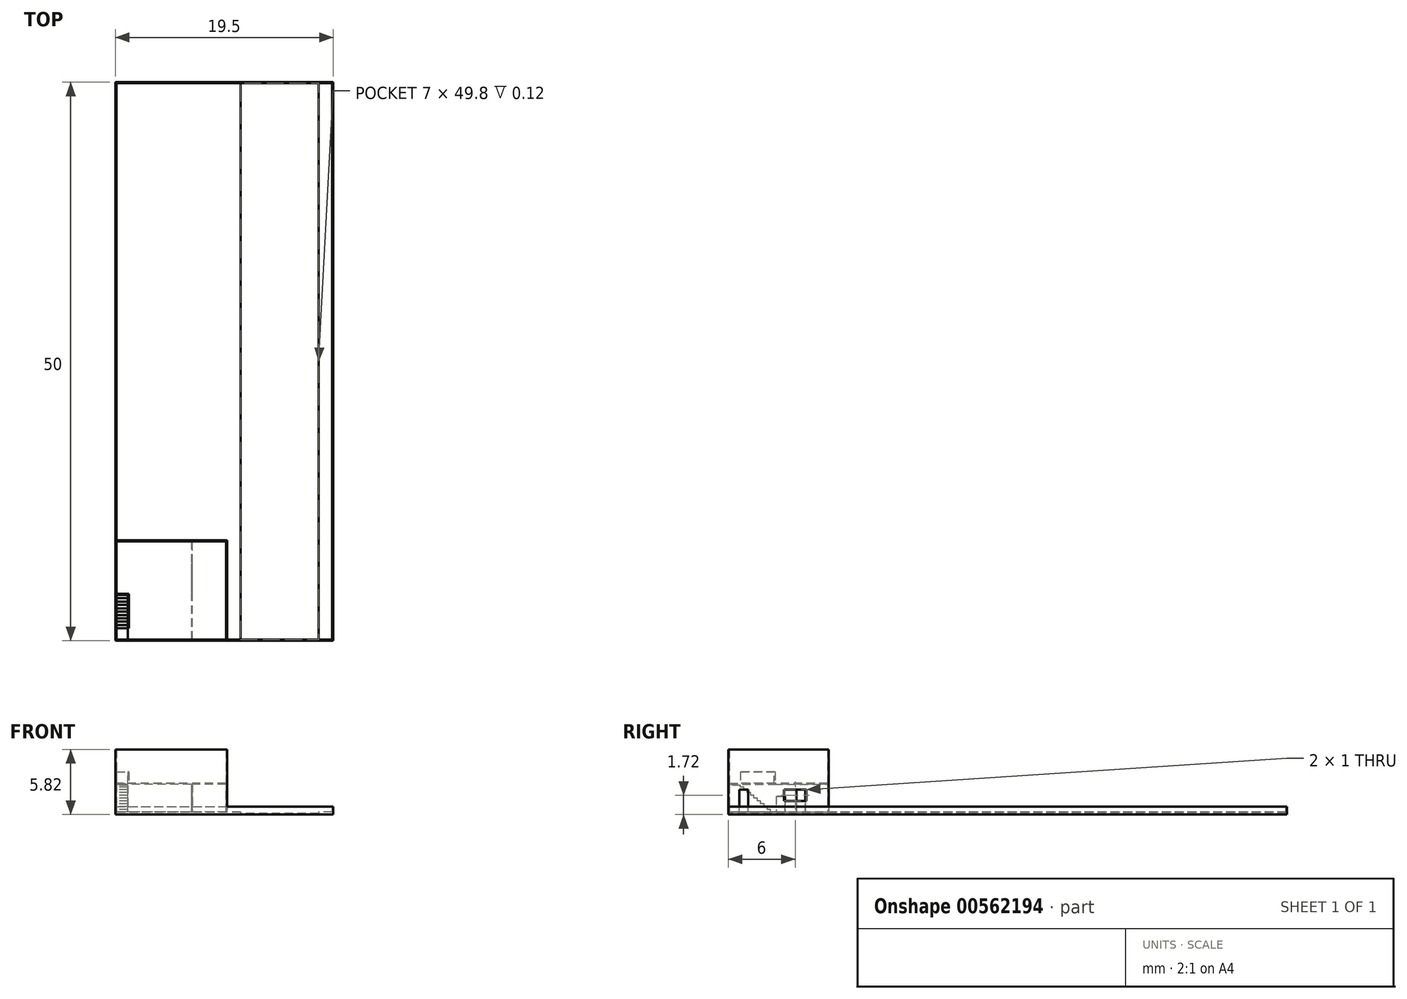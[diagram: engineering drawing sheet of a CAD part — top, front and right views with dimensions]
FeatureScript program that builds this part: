
annotation { "Feature Type Name" : "Feature", "Feature Type Description" : "" }
export const myFeature = defineFeature(function(context is Context, id is Id, definition is map)
    precondition{}
    {
        {
            var Q0;
            Q0=qCreatedBy(makeId("Top.planeOp"),FACE);
            var sketch = newSketch(context, id + "F0", { "sketchPlane" : qUnion([Q0])});
            skLineSegment(sketch, "E0.bottom", {"start": v(0, 0) * mm, "end": v(19.5, 0) * mm});
            skLineSegment(sketch, "E0.top", {"start": v(0, 50) * mm, "end": v(19.5, 50) * mm});
            skLineSegment(sketch, "E0.left", {"start": v(0, 0) * mm, "end": v(0, 50) * mm});
            skLineSegment(sketch, "E0.right", {"start": v(19.5, 0) * mm, "end": v(19.5, 50) * mm});
            skLineSegment(sketch, "E1", {"start": v(11.2, 50) * mm, "end": v(11.2, 0) * mm});
            skLineSegment(sketch, "E2", {"start": v(18.2, 50) * mm, "end": v(18.2, 0) * mm});
            skLineSegment(sketch, "E3", {"start": v(10, 0) * mm, "end": v(10, 50) * mm});
            skLineSegment(sketch, "E4", {"start": v(0, 49.9) * mm, "end": v(19.5, 49.9) * mm});
            skLineSegment(sketch, "E5", {"start": v(19.4, 50) * mm, "end": v(19.4, 0) * mm});
            skLineSegment(sketch, "E6", {"start": v(19.5, 0.1) * mm, "end": v(0, 0.1) * mm});
            skSolve(sketch);
        }
        {
            var Q0;
            {var subQ0=sQuery(id+"F0.wireOp",EDGE,"E4");var subQ1=sQuery(id+"F0.wireOp",EDGE,"E1");var subQ2=makeQuery(id+"F0.imprint","INTERSECT",VERTEX,{"derivedFrom":[subQ1,subQ0]});Q0=makeQuery(id+"F0.imprint","IMPRINT",FACE,{"disambiguationData":[TD([[makeQuery(id+"F0.imprint","IMPRINT",EDGE,{"disambiguationData":[TD([[subQ2,-1.0]])],"derivedFrom":subQ1}),-1.0]])]});}
            var Q1;
            {var subQ0=sQuery(id+"F0.wireOp",EDGE,"E4");var subQ1=sQuery(id+"F0.wireOp",EDGE,"E0.left");var subQ2=makeQuery(id+"F0.imprint","INTERSECT",VERTEX,{"derivedFrom":[subQ1,subQ0]});Q1=makeQuery(id+"F0.imprint","IMPRINT",FACE,{"disambiguationData":[TD([[makeQuery(id+"F0.imprint","IMPRINT",EDGE,{"disambiguationData":[TD([[subQ2,1.0]])],"derivedFrom":subQ1}),-1.0]])]});}
            var Q2;
            {var subQ0=sQuery(id+"F0.wireOp",EDGE,"E4");var subQ1=sQuery(id+"F0.wireOp",EDGE,"E2");var subQ2=makeQuery(id+"F0.imprint","INTERSECT",VERTEX,{"derivedFrom":[subQ1,subQ0]});Q2=makeQuery(id+"F0.imprint","IMPRINT",FACE,{"disambiguationData":[TD([[makeQuery(id+"F0.imprint","IMPRINT",EDGE,{"disambiguationData":[TD([[subQ2,-1.0]])],"derivedFrom":subQ1}),1.0]])]});}
            extrude(context, id + "F1", {"entities" : qUnion([Q0, Q1, Q2]), "depth" : 0.12 * mm, "offsetDistance" : 25 * mm});
        }
        {
            var Q0;
            {var subQ0=sQuery(id+"F0.wireOp",EDGE,"E4");var subQ1=sQuery(id+"F0.wireOp",EDGE,"E0.left");var subQ2=makeQuery(id+"F0.imprint","INTERSECT",VERTEX,{"derivedFrom":[subQ1,subQ0]});Q0=makeQuery(id+"F0.imprint","IMPRINT",FACE,{"disambiguationData":[TD([[makeQuery(id+"F0.imprint","IMPRINT",EDGE,{"disambiguationData":[TD([[subQ2,1.0]])],"derivedFrom":subQ1}),-1.0]])]});}
            var Q1;
            {var subQ0=sQuery(id+"F0.wireOp",EDGE,"E4");var subQ1=sQuery(id+"F0.wireOp",EDGE,"E1");var subQ2=makeQuery(id+"F0.imprint","INTERSECT",VERTEX,{"derivedFrom":[subQ1,subQ0]});Q1=makeQuery(id+"F0.imprint","IMPRINT",FACE,{"disambiguationData":[TD([[makeQuery(id+"F0.imprint","IMPRINT",EDGE,{"disambiguationData":[TD([[subQ2,-1.0]])],"derivedFrom":subQ1}),-1.0]])]});}
            var Q2;
            {var subQ0=sQuery(id+"F0.wireOp",EDGE,"E4");var subQ1=sQuery(id+"F0.wireOp",EDGE,"E2");var subQ2=makeQuery(id+"F0.imprint","INTERSECT",VERTEX,{"derivedFrom":[subQ1,subQ0]});Q2=makeQuery(id+"F0.imprint","IMPRINT",FACE,{"disambiguationData":[TD([[makeQuery(id+"F0.imprint","IMPRINT",EDGE,{"disambiguationData":[TD([[subQ2,-1.0]])],"derivedFrom":subQ1}),1.0]])]});}
            var Q3;
            {var subQ0=sQuery(id+"F0.wireOp",EDGE,"E4");var subQ1=sQuery(id+"F0.wireOp",EDGE,"E1");var subQ2=makeQuery(id+"F0.imprint","INTERSECT",VERTEX,{"derivedFrom":[subQ1,subQ0]});Q3=makeQuery(id+"F0.imprint","IMPRINT",FACE,{"disambiguationData":[TD([[makeQuery(id+"F0.imprint","IMPRINT",EDGE,{"disambiguationData":[TD([[subQ2,-1.0]])],"derivedFrom":subQ1}),1.0]])]});}
            var Q4;
            {var subQ0=sQuery(id+"F0.wireOp",EDGE,"E1");var subQ1=sQuery(id+"F0.wireOp",EDGE,"E0.bottom");var subQ2=makeQuery(id+"F0.imprint","INTERSECT",VERTEX,{"derivedFrom":[subQ1,subQ0]});Q4=makeQuery(id+"F0.imprint","IMPRINT",FACE,{"disambiguationData":[TD([[makeQuery(id+"F0.imprint","IMPRINT",EDGE,{"disambiguationData":[TD([[subQ2,-1.0]])],"derivedFrom":subQ1}),1.0]])]});}
            var Q5;
            {var subQ0=sQuery(id+"F0.wireOp",EDGE,"E1");var subQ1=sQuery(id+"F0.wireOp",EDGE,"E0.bottom");var subQ2=makeQuery(id+"F0.imprint","INTERSECT",VERTEX,{"derivedFrom":[subQ1,subQ0]});Q5=makeQuery(id+"F0.imprint","IMPRINT",FACE,{"disambiguationData":[TD([[makeQuery(id+"F0.imprint","IMPRINT",EDGE,{"disambiguationData":[TD([[subQ2,1.0]])],"derivedFrom":subQ1}),1.0]])]});}
            var Q6;
            {var subQ0=sQuery(id+"F0.wireOp",EDGE,"E2");var subQ1=sQuery(id+"F0.wireOp",EDGE,"E0.bottom");var subQ2=makeQuery(id+"F0.imprint","INTERSECT",VERTEX,{"derivedFrom":[subQ1,subQ0]});Q6=makeQuery(id+"F0.imprint","IMPRINT",FACE,{"disambiguationData":[TD([[makeQuery(id+"F0.imprint","IMPRINT",EDGE,{"disambiguationData":[TD([[subQ2,-1.0]])],"derivedFrom":subQ1}),1.0]])]});}
            var Q7;
            {var subQ0=sQuery(id+"F0.wireOp",EDGE,"E4");var subQ1=sQuery(id+"F0.wireOp",EDGE,"E0.right");var subQ2=makeQuery(id+"F0.imprint","INTERSECT",VERTEX,{"derivedFrom":[subQ1,subQ0]});Q7=makeQuery(id+"F0.imprint","IMPRINT",FACE,{"disambiguationData":[TD([[makeQuery(id+"F0.imprint","IMPRINT",EDGE,{"disambiguationData":[TD([[subQ2,1.0]])],"derivedFrom":subQ1}),1.0]])]});}
            var Q8;
            {var subQ0=sQuery(id+"F0.wireOp",EDGE,"E0.right");var subQ1=sQuery(id+"F0.wireOp",EDGE,"E0.bottom");var subQ2=makeQuery(id+"F0.imprint","INTERSECT",VERTEX,{"derivedFrom":[subQ1,subQ0]});Q8=makeQuery(id+"F0.imprint","IMPRINT",FACE,{"disambiguationData":[TD([[makeQuery(id+"F0.imprint","IMPRINT",EDGE,{"disambiguationData":[TD([[subQ2,1.0]])],"derivedFrom":subQ1}),1.0]])]});}
            var Q9;
            {var subQ0=sQuery(id+"F0.wireOp",EDGE,"E0.left");var subQ1=sQuery(id+"F0.wireOp",EDGE,"E0.bottom");var subQ2=makeQuery(id+"F0.imprint","INTERSECT",VERTEX,{"derivedFrom":[subQ1,subQ0]});Q9=makeQuery(id+"F0.imprint","IMPRINT",FACE,{"disambiguationData":[TD([[makeQuery(id+"F0.imprint","IMPRINT",EDGE,{"disambiguationData":[TD([[subQ2,-1.0]])],"derivedFrom":subQ1}),1.0]])]});}
            var Q10;
            {var subQ0=sQuery(id+"F0.wireOp",EDGE,"E0.right");var subQ1=sQuery(id+"F0.wireOp",EDGE,"E0.top");var subQ2=makeQuery(id+"F0.imprint","INTERSECT",VERTEX,{"derivedFrom":[subQ1,subQ0]});Q10=makeQuery(id+"F0.imprint","IMPRINT",FACE,{"disambiguationData":[TD([[makeQuery(id+"F0.imprint","IMPRINT",EDGE,{"disambiguationData":[TD([[subQ2,1.0]])],"derivedFrom":subQ1}),-1.0]])]});}
            var Q11;
            {var subQ0=sQuery(id+"F0.wireOp",EDGE,"E2");var subQ1=sQuery(id+"F0.wireOp",EDGE,"E0.top");var subQ2=makeQuery(id+"F0.imprint","INTERSECT",VERTEX,{"derivedFrom":[subQ1,subQ0]});Q11=makeQuery(id+"F0.imprint","IMPRINT",FACE,{"disambiguationData":[TD([[makeQuery(id+"F0.imprint","IMPRINT",EDGE,{"disambiguationData":[TD([[subQ2,-1.0]])],"derivedFrom":subQ1}),-1.0]])]});}
            var Q12;
            {var subQ0=sQuery(id+"F0.wireOp",EDGE,"E1");var subQ1=sQuery(id+"F0.wireOp",EDGE,"E0.top");var subQ2=makeQuery(id+"F0.imprint","INTERSECT",VERTEX,{"derivedFrom":[subQ1,subQ0]});Q12=makeQuery(id+"F0.imprint","IMPRINT",FACE,{"disambiguationData":[TD([[makeQuery(id+"F0.imprint","IMPRINT",EDGE,{"disambiguationData":[TD([[subQ2,-1.0]])],"derivedFrom":subQ1}),-1.0]])]});}
            var Q13;
            {var subQ0=sQuery(id+"F0.wireOp",EDGE,"E1");var subQ1=sQuery(id+"F0.wireOp",EDGE,"E0.top");var subQ2=makeQuery(id+"F0.imprint","INTERSECT",VERTEX,{"derivedFrom":[subQ1,subQ0]});Q13=makeQuery(id+"F0.imprint","IMPRINT",FACE,{"disambiguationData":[TD([[makeQuery(id+"F0.imprint","IMPRINT",EDGE,{"disambiguationData":[TD([[subQ2,1.0]])],"derivedFrom":subQ1}),-1.0]])]});}
            var Q14;
            {var subQ0=sQuery(id+"F0.wireOp",EDGE,"E0.left");var subQ1=sQuery(id+"F0.wireOp",EDGE,"E0.top");var subQ2=makeQuery(id+"F0.imprint","INTERSECT",VERTEX,{"derivedFrom":[subQ1,subQ0]});Q14=makeQuery(id+"F0.imprint","IMPRINT",FACE,{"disambiguationData":[TD([[makeQuery(id+"F0.imprint","IMPRINT",EDGE,{"disambiguationData":[TD([[subQ2,-1.0]])],"derivedFrom":subQ1}),-1.0]])]});}
            var Q15;
            Q15=makeQuery(id+"F1.opExtrude","CAP_FACE",FACE,{"disambiguationData":[OSD([sQuery(id+"F0.wireOp",EDGE,"E2"),sQuery(id+"F0.wireOp",EDGE,"E4"),sQuery(id+"F0.wireOp",EDGE,"E5"),sQuery(id+"F0.wireOp",EDGE,"E6")])],"isStart":false});
            var Q16;
            Q16=makeQuery(id+"F1.opExtrude","CAP_FACE",FACE,{"disambiguationData":[OSD([sQuery(id+"F0.wireOp",EDGE,"E0.left"),sQuery(id+"F0.wireOp",EDGE,"E1"),sQuery(id+"F0.wireOp",EDGE,"E4"),sQuery(id+"F0.wireOp",EDGE,"E6")])],"isStart":false});
            extrude(context, id + "F2", {"entities" : qUnion([Q0, Q1, Q2, Q3, Q4, Q5, Q6, Q7, Q8, Q9, Q10, Q11, Q12, Q13, Q14, Q15, Q16]), "operationType" : NewBodyOperationType.ADD, "oppositeDirection" : true, "depth" : 0.1 * mm, "offsetDistance" : 25 * mm});
        }
        {
            var Q0;
            {var subQ0=sQuery(id+"F0.wireOp",EDGE,"E1");var subQ1=sQuery(id+"F0.wireOp",EDGE,"E0.top");var subQ2=makeQuery(id+"F0.imprint","INTERSECT",VERTEX,{"derivedFrom":[subQ1,subQ0]});Q0=makeQuery(id+"F0.imprint","IMPRINT",FACE,{"disambiguationData":[TD([[makeQuery(id+"F0.imprint","IMPRINT",EDGE,{"disambiguationData":[TD([[subQ2,1.0]])],"derivedFrom":subQ1}),-1.0]])]});}
            var Q1;
            {var subQ0=sQuery(id+"F0.wireOp",EDGE,"E0.left");var subQ1=sQuery(id+"F0.wireOp",EDGE,"E0.top");var subQ2=makeQuery(id+"F0.imprint","INTERSECT",VERTEX,{"derivedFrom":[subQ1,subQ0]});Q1=makeQuery(id+"F0.imprint","IMPRINT",FACE,{"disambiguationData":[TD([[makeQuery(id+"F0.imprint","IMPRINT",EDGE,{"disambiguationData":[TD([[subQ2,-1.0]])],"derivedFrom":subQ1}),-1.0]])]});}
            var Q2;
            {var subQ0=sQuery(id+"F0.wireOp",EDGE,"E1");var subQ1=sQuery(id+"F0.wireOp",EDGE,"E0.top");var subQ2=makeQuery(id+"F0.imprint","INTERSECT",VERTEX,{"derivedFrom":[subQ1,subQ0]});Q2=makeQuery(id+"F0.imprint","IMPRINT",FACE,{"disambiguationData":[TD([[makeQuery(id+"F0.imprint","IMPRINT",EDGE,{"disambiguationData":[TD([[subQ2,-1.0]])],"derivedFrom":subQ1}),-1.0]])]});}
            var Q3;
            {var subQ0=sQuery(id+"F0.wireOp",EDGE,"E2");var subQ1=sQuery(id+"F0.wireOp",EDGE,"E0.top");var subQ2=makeQuery(id+"F0.imprint","INTERSECT",VERTEX,{"derivedFrom":[subQ1,subQ0]});Q3=makeQuery(id+"F0.imprint","IMPRINT",FACE,{"disambiguationData":[TD([[makeQuery(id+"F0.imprint","IMPRINT",EDGE,{"disambiguationData":[TD([[subQ2,-1.0]])],"derivedFrom":subQ1}),-1.0]])]});}
            var Q4;
            {var subQ0=sQuery(id+"F0.wireOp",EDGE,"E4");var subQ1=sQuery(id+"F0.wireOp",EDGE,"E0.right");var subQ2=makeQuery(id+"F0.imprint","INTERSECT",VERTEX,{"derivedFrom":[subQ1,subQ0]});Q4=makeQuery(id+"F0.imprint","IMPRINT",FACE,{"disambiguationData":[TD([[makeQuery(id+"F0.imprint","IMPRINT",EDGE,{"disambiguationData":[TD([[subQ2,1.0]])],"derivedFrom":subQ1}),1.0]])]});}
            var Q5;
            {var subQ0=sQuery(id+"F0.wireOp",EDGE,"E0.right");var subQ1=sQuery(id+"F0.wireOp",EDGE,"E0.top");var subQ2=makeQuery(id+"F0.imprint","INTERSECT",VERTEX,{"derivedFrom":[subQ1,subQ0]});Q5=makeQuery(id+"F0.imprint","IMPRINT",FACE,{"disambiguationData":[TD([[makeQuery(id+"F0.imprint","IMPRINT",EDGE,{"disambiguationData":[TD([[subQ2,1.0]])],"derivedFrom":subQ1}),-1.0]])]});}
            var Q6;
            {var subQ0=sQuery(id+"F0.wireOp",EDGE,"E0.right");var subQ1=sQuery(id+"F0.wireOp",EDGE,"E0.bottom");var subQ2=makeQuery(id+"F0.imprint","INTERSECT",VERTEX,{"derivedFrom":[subQ1,subQ0]});Q6=makeQuery(id+"F0.imprint","IMPRINT",FACE,{"disambiguationData":[TD([[makeQuery(id+"F0.imprint","IMPRINT",EDGE,{"disambiguationData":[TD([[subQ2,1.0]])],"derivedFrom":subQ1}),1.0]])]});}
            var Q7;
            {var subQ0=sQuery(id+"F0.wireOp",EDGE,"E2");var subQ1=sQuery(id+"F0.wireOp",EDGE,"E0.bottom");var subQ2=makeQuery(id+"F0.imprint","INTERSECT",VERTEX,{"derivedFrom":[subQ1,subQ0]});Q7=makeQuery(id+"F0.imprint","IMPRINT",FACE,{"disambiguationData":[TD([[makeQuery(id+"F0.imprint","IMPRINT",EDGE,{"disambiguationData":[TD([[subQ2,-1.0]])],"derivedFrom":subQ1}),1.0]])]});}
            var Q8;
            {var subQ0=sQuery(id+"F0.wireOp",EDGE,"E1");var subQ1=sQuery(id+"F0.wireOp",EDGE,"E0.bottom");var subQ2=makeQuery(id+"F0.imprint","INTERSECT",VERTEX,{"derivedFrom":[subQ1,subQ0]});Q8=makeQuery(id+"F0.imprint","IMPRINT",FACE,{"disambiguationData":[TD([[makeQuery(id+"F0.imprint","IMPRINT",EDGE,{"disambiguationData":[TD([[subQ2,-1.0]])],"derivedFrom":subQ1}),1.0]])]});}
            var Q9;
            {var subQ0=sQuery(id+"F0.wireOp",EDGE,"E0.left");var subQ1=sQuery(id+"F0.wireOp",EDGE,"E0.bottom");var subQ2=makeQuery(id+"F0.imprint","INTERSECT",VERTEX,{"derivedFrom":[subQ1,subQ0]});Q9=makeQuery(id+"F0.imprint","IMPRINT",FACE,{"disambiguationData":[TD([[makeQuery(id+"F0.imprint","IMPRINT",EDGE,{"disambiguationData":[TD([[subQ2,-1.0]])],"derivedFrom":subQ1}),1.0]])]});}
            var Q10;
            {var subQ0=sQuery(id+"F0.wireOp",EDGE,"E1");var subQ1=sQuery(id+"F0.wireOp",EDGE,"E0.bottom");var subQ2=makeQuery(id+"F0.imprint","INTERSECT",VERTEX,{"derivedFrom":[subQ1,subQ0]});Q10=makeQuery(id+"F0.imprint","IMPRINT",FACE,{"disambiguationData":[TD([[makeQuery(id+"F0.imprint","IMPRINT",EDGE,{"disambiguationData":[TD([[subQ2,1.0]])],"derivedFrom":subQ1}),1.0]])]});}
            extrude(context, id + "F3", {"entities" : qUnion([Q0, Q1, Q2, Q3, Q4, Q5, Q6, Q7, Q8, Q9, Q10]), "operationType" : NewBodyOperationType.ADD, "depth" : 0.6 * mm, "offsetDistance" : 25 * mm});
        }
        {
            var Q0;
            Q0=makeQuery(id+"F1.opExtrude","CAP_FACE",FACE,{"disambiguationData":[OSD([sQuery(id+"F0.wireOp",EDGE,"E0.left"),sQuery(id+"F0.wireOp",EDGE,"E1"),sQuery(id+"F0.wireOp",EDGE,"E4"),sQuery(id+"F0.wireOp",EDGE,"E6")])],"isStart":false});
            var sketch = newSketch(context, id + "F4", { "sketchPlane" : qUnion([Q0])});
            skLineSegment(sketch, "E7.bottom", {"start": v(10, 0) * mm, "end": v(0, 0) * mm});
            skLineSegment(sketch, "E7.top", {"start": v(10, 9) * mm, "end": v(0, 9) * mm});
            skLineSegment(sketch, "E7.left", {"start": v(10, 0) * mm, "end": v(10, 9) * mm});
            skLineSegment(sketch, "E7.right", {"start": v(0, 0) * mm, "end": v(0, 9) * mm});
            skLineSegment(sketch, "E8.0", {"start": v(0.1, 0.1) * mm, "end": v(0.1, 8.9) * mm});
            skLineSegment(sketch, "E8.1", {"start": v(9.9, 0.1) * mm, "end": v(0.1, 0.1) * mm});
            skLineSegment(sketch, "E8.2", {"start": v(9.9, 0.1) * mm, "end": v(9.9, 8.9) * mm});
            skLineSegment(sketch, "E8.3", {"start": v(9.9, 8.9) * mm, "end": v(0.1, 8.9) * mm});
            skLineSegment(sketch, "E9", {"start": v(6.9, 0.1) * mm, "end": v(6.9, 8.9) * mm});
            skLineSegment(sketch, "E10", {"start": v(6.8, 8.9) * mm, "end": v(6.8, 0.1) * mm});
            skSolve(sketch);
        }
        {
            var Q0;
            Q0 = qSketchRegion(id + "F4", true);
            var Q1;
            {var subQ0=sQuery(id+"F4.wireOp",EDGE,"E9");Q1=makeQuery(id+"F4.imprint","IMPRINT",FACE,{"disambiguationData":[TD([[makeQuery(id+"F4.imprint","IMPRINT",EDGE,{"derivedFrom":subQ0}),1.0]])]});}
            extrude(context, id + "F5", {"entities" : qUnion([Q0, Q1]), "operationType" : NewBodyOperationType.ADD, "depth" : 2.5 * mm, "offsetDistance" : 25 * mm});
        }
        {
            var Q0;
            Q0=makeQuery(id+"F5.opExtrude","SWEPT_FACE",FACE,{"disambiguationData":[OSD([sQuery(id+"F4.wireOp",EDGE,"E7.left")])]});
            var sketch = newSketch(context, id + "F6", { "sketchPlane" : qUnion([Q0])});
            skLineSegment(sketch, "E11.bottom", {"start": v(1, 0.12) * mm, "end": v(1.8, 0.12) * mm});
            skLineSegment(sketch, "E11.top", {"start": v(1, 2.12) * mm, "end": v(1.8, 2.12) * mm});
            skLineSegment(sketch, "E11.left", {"start": v(1, 0.12) * mm, "end": v(1, 2.12) * mm});
            skLineSegment(sketch, "E11.right", {"start": v(1.8, 0.12) * mm, "end": v(1.8, 2.12) * mm});
            skLineSegment(sketch, "E12.bottom", {"start": v(5, 2.12) * mm, "end": v(7, 2.12) * mm});
            skLineSegment(sketch, "E12.top", {"start": v(5, 1.12) * mm, "end": v(7, 1.12) * mm});
            skLineSegment(sketch, "E12.left", {"start": v(5, 2.12) * mm, "end": v(5, 1.12) * mm});
            skLineSegment(sketch, "E12.right", {"start": v(7, 2.12) * mm, "end": v(7, 1.12) * mm});
            skSolve(sketch);
        }
        {
            var Q0;
            Q0=makeQuery(id+"F6.imprint","IMPRINT",FACE,{"disambiguationData":[TD([[makeQuery(id+"F6.imprint","IMPRINT",EDGE,{"derivedFrom":sQuery(id+"F6.wireOp",EDGE,"E11.bottom")}),1.0]])]});
            var Q1;
            Q1=makeQuery(id+"F6.imprint","IMPRINT",FACE,{"disambiguationData":[TD([[makeQuery(id+"F6.imprint","IMPRINT",EDGE,{"derivedFrom":sQuery(id+"F6.wireOp",EDGE,"E12.bottom")}),-1.0]])]});
            extrude(context, id + "F7", {"entities" : qUnion([Q0, Q1]), "operationType" : NewBodyOperationType.REMOVE, "endBound" : BoundingType.UP_TO_NEXT, "oppositeDirection" : true, "depth" : 0.1 * mm, "offsetDistance" : 25 * mm});
        }
        {
            var Q0;
            Q0=makeQuery(id+"F5.opExtrude","SWEPT_FACE",FACE,{"disambiguationData":[OSD([sQuery(id+"F4.wireOp",EDGE,"E9")])]});
            var sketch = newSketch(context, id + "F8", { "sketchPlane" : qUnion([Q0])});
            skLineSegment(sketch, "E13.bottom", {"start": v(6.1, 0.12) * mm, "end": v(6.9, 0.12) * mm});
            skLineSegment(sketch, "E13.top", {"start": v(6.1, 2.12) * mm, "end": v(6.9, 2.12) * mm});
            skLineSegment(sketch, "E13.left", {"start": v(6.1, 0.12) * mm, "end": v(6.1, 2.12) * mm});
            skLineSegment(sketch, "E13.right", {"start": v(6.9, 0.12) * mm, "end": v(6.9, 2.12) * mm});
            skLineSegment(sketch, "E14.bottom", {"start": v(4.3, 0.12) * mm, "end": v(5.1, 0.12) * mm});
            skLineSegment(sketch, "E14.top", {"start": v(4.3, 1.52) * mm, "end": v(5.1, 1.52) * mm});
            skLineSegment(sketch, "E14.left", {"start": v(4.3, 0.12) * mm, "end": v(4.3, 1.52) * mm});
            skLineSegment(sketch, "E14.right", {"start": v(5.1, 0.12) * mm, "end": v(5.1, 1.52) * mm});
            skSolve(sketch);
        }
        {
            var Q0;
            Q0=makeQuery(id+"F8.imprint","IMPRINT",FACE,{"disambiguationData":[TD([[makeQuery(id+"F8.imprint","IMPRINT",EDGE,{"derivedFrom":sQuery(id+"F8.wireOp",EDGE,"E14.bottom")}),1.0]])]});
            var Q1;
            Q1=makeQuery(id+"F8.imprint","IMPRINT",FACE,{"disambiguationData":[TD([[makeQuery(id+"F8.imprint","IMPRINT",EDGE,{"derivedFrom":sQuery(id+"F8.wireOp",EDGE,"E13.bottom")}),1.0]])]});
            extrude(context, id + "F9", {"entities" : qUnion([Q0, Q1]), "operationType" : NewBodyOperationType.REMOVE, "endBound" : BoundingType.UP_TO_NEXT, "oppositeDirection" : true, "depth" : 25 * mm, "offsetDistance" : 25 * mm});
        }
        {
            var Q0;
            Q0=makeQuery(id+"F5.opExtrude","SWEPT_FACE",FACE,{"disambiguationData":[OSD([sQuery(id+"F4.wireOp",EDGE,"E8.0")])]});
            var sketch = newSketch(context, id + "F10", { "sketchPlane" : qUnion([Q0])});
            skLineSegment(sketch, "E15", {"start": v(3.8, 0.12) * mm, "end": v(3.8, 0.37) * mm});
            skLineSegment(sketch, "E16", {"start": v(3.8, 0.37) * mm, "end": v(3.5, 0.37) * mm});
            skLineSegment(sketch, "E17", {"start": v(3.5, 0.37) * mm, "end": v(3.5, 0.62) * mm});
            skLineSegment(sketch, "E18", {"start": v(3.5, 0.62) * mm, "end": v(3.2, 0.62) * mm});
            skLineSegment(sketch, "E19", {"start": v(3.2, 0.62) * mm, "end": v(3.2, 0.87) * mm});
            skLineSegment(sketch, "E20", {"start": v(3.2, 0.87) * mm, "end": v(2.9, 0.87) * mm});
            skLineSegment(sketch, "E21", {"start": v(2.9, 0.87) * mm, "end": v(2.9, 1.12) * mm});
            skLineSegment(sketch, "E22", {"start": v(2.9, 1.12) * mm, "end": v(2.6, 1.12) * mm});
            skLineSegment(sketch, "E23", {"start": v(2.6, 1.12) * mm, "end": v(2.6, 1.37) * mm});
            skLineSegment(sketch, "E24", {"start": v(2.6, 1.37) * mm, "end": v(2.3, 1.37) * mm});
            skLineSegment(sketch, "E25", {"start": v(2.3, 1.37) * mm, "end": v(2.3, 1.62) * mm});
            skLineSegment(sketch, "E26", {"start": v(2.3, 1.62) * mm, "end": v(2, 1.62) * mm});
            skLineSegment(sketch, "E27", {"start": v(2, 1.62) * mm, "end": v(2, 1.87) * mm});
            skLineSegment(sketch, "E28", {"start": v(2, 1.87) * mm, "end": v(1.7, 1.87) * mm});
            skLineSegment(sketch, "E29", {"start": v(1.7, 1.87) * mm, "end": v(1.7, 2.12) * mm});
            skLineSegment(sketch, "E30", {"start": v(1.7, 2.12) * mm, "end": v(1.4, 2.12) * mm});
            skLineSegment(sketch, "E31", {"start": v(1.4, 2.12) * mm, "end": v(1.4, 2.37) * mm});
            skLineSegment(sketch, "E32", {"start": v(1.4, 2.37) * mm, "end": v(1.1, 2.37) * mm});
            skLineSegment(sketch, "E33", {"start": v(1.1, 2.37) * mm, "end": v(1.1, 2.62) * mm});
            skSolve(sketch);
        }
        {
            var Q0;
            {var subQ0=sQuery(id+"F10.wireOp",EDGE,"E15");Q0=makeQuery(id+"F10.imprint","IMPRINT",FACE,{"disambiguationData":[TD([[makeQuery(id+"F10.imprint","IMPRINT",EDGE,{"derivedFrom":subQ0}),1.0]])]});}
            extrude(context, id + "F11", {"entities" : qUnion([Q0]), "operationType" : NewBodyOperationType.ADD, "depth" : 1 * mm, "offsetDistance" : 25 * mm});
        }
        {
            var Q0;
            {var subQ0=sQuery(id+"F4.wireOp",EDGE,"E8.1");var subQ1=sQuery(id+"F4.wireOp",EDGE,"E8.0");var subQ2=makeQuery(id+"F5.opExtrude","CAP_EDGE",EDGE,{"disambiguationData":[OSD([subQ1])],"isStart":false});Q0=makeQuery(id+"F11.boolean.opBoolean","MERGE",FACE,{"derivedFrom":[makeQuery(id+"F5.opExtrude","CAP_FACE",FACE,{"disambiguationData":[OSD([sQuery(id+"F4.wireOp",EDGE,"E7.bottom"),sQuery(id+"F4.wireOp",EDGE,"E7.top"),sQuery(id+"F4.wireOp",EDGE,"E7.left"),sQuery(id+"F4.wireOp",EDGE,"E7.right"),subQ1,subQ0,sQuery(id+"F4.wireOp",EDGE,"E8.2"),sQuery(id+"F4.wireOp",EDGE,"E8.3"),sQuery(id+"F4.wireOp",EDGE,"E9"),sQuery(id+"F4.wireOp",EDGE,"E10")])],"isStart":false}),makeQuery(id+"F11.opExtrude","SWEPT_FACE",FACE,{"disambiguationData":[OSD([subQ1]),TDD([makeQuery(id+"F10.imprint","IMPRINT",EDGE,{"disambiguationData":[TD([[makeQuery(id+"F10.imprint","INTERSECT",VERTEX,{"derivedFrom":[subQ2,sQuery(id+"F10.wireOp",EDGE,"E33")]}),1.0]])],"derivedFrom":subQ2})])]})]});}
            var sketch = newSketch(context, id + "F12", { "sketchPlane" : qUnion([Q0])});
            skLineSegment(sketch, "E34.bottom", {"start": v(10, 0) * mm, "end": v(0, 0) * mm});
            skLineSegment(sketch, "E34.top", {"start": v(10, 9) * mm, "end": v(0, 9) * mm});
            skLineSegment(sketch, "E34.left", {"start": v(10, 0) * mm, "end": v(10, 9) * mm});
            skLineSegment(sketch, "E34.right", {"start": v(0, 0) * mm, "end": v(0, 9) * mm});
            skSolve(sketch);
        }
        {
            var Q0;
            Q0=makeQuery(id+"F12.imprint","IMPRINT",FACE,{"disambiguationData":[TD([[makeQuery(id+"F12.imprint","IMPRINT",EDGE,{"derivedFrom":sQuery(id+"F12.wireOp",EDGE,"E34.bottom")}),-1.0]])]});
            var Q1;
            {var subQ5=sQuery(id+"F4.wireOp",EDGE,"E10");Q1=makeQuery(id+"F12.imprint","IMPRINT",FACE,{"disambiguationData":[TD([[makeQuery(id+"F12.imprint","IMPRINT",EDGE,{"derivedFrom":makeQuery(id+"F5.opExtrude","CAP_EDGE",EDGE,{"disambiguationData":[OSD([subQ5])],"isStart":false})}),-1.0]])]});}
            var Q2;
            {var subQ0=sQuery(id+"F4.wireOp",EDGE,"E8.2");Q2=makeQuery(id+"F12.imprint","IMPRINT",FACE,{"disambiguationData":[TD([[makeQuery(id+"F12.imprint","IMPRINT",EDGE,{"derivedFrom":makeQuery(id+"F5.opExtrude","CAP_EDGE",EDGE,{"disambiguationData":[OSD([subQ0])],"isStart":false})}),1.0]])]});}
            extrude(context, id + "F13", {"entities" : qUnion([Q0, Q1, Q2]), "operationType" : NewBodyOperationType.ADD, "depth" : 0.1 * mm, "offsetDistance" : 25 * mm});
        }
        {
            var Q0;
            Q0=makeQuery(id+"F13.opExtrude","CAP_FACE",FACE,{"disambiguationData":[OSD([sQuery(id+"F12.wireOp",EDGE,"E34.bottom"),sQuery(id+"F12.wireOp",EDGE,"E34.top"),sQuery(id+"F12.wireOp",EDGE,"E34.left"),sQuery(id+"F12.wireOp",EDGE,"E34.right")])],"isStart":false});
            var sketch = newSketch(context, id + "F14", { "sketchPlane" : qUnion([Q0])});
            skLineSegment(sketch, "E35.0", {"start": v(0.1, 8.9) * mm, "end": v(0.1, 0.1) * mm});
            skLineSegment(sketch, "E35.1", {"start": v(9.9, 8.9) * mm, "end": v(0.1, 8.9) * mm});
            skLineSegment(sketch, "E35.2", {"start": v(9.9, 0.1) * mm, "end": v(9.9, 8.9) * mm});
            skLineSegment(sketch, "E35.3", {"start": v(0.1, 0.1) * mm, "end": v(9.9, 0.1) * mm});
            skSolve(sketch);
        }
        {
            var Q0;
            Q0=makeQuery(id+"F14.imprint","IMPRINT",FACE,{"disambiguationData":[TD([[makeQuery(id+"F14.imprint","IMPRINT",EDGE,{"derivedFrom":sQuery(id+"F14.wireOp",EDGE,"E35.0")}),-1.0]])]});
            extrude(context, id + "F15", {"entities" : qUnion([Q0]), "operationType" : NewBodyOperationType.ADD, "depth" : 3 * mm, "offsetDistance" : 25 * mm});
        }
        {
            var Q0;
            Q0=makeQuery(id+"F13.opExtrude","CAP_FACE",FACE,{"disambiguationData":[OSD([sQuery(id+"F12.wireOp",EDGE,"E34.bottom"),sQuery(id+"F12.wireOp",EDGE,"E34.top"),sQuery(id+"F12.wireOp",EDGE,"E34.left"),sQuery(id+"F12.wireOp",EDGE,"E34.right")])],"isStart":false});
            var sketch = newSketch(context, id + "F16", { "sketchPlane" : qUnion([Q0])});
            skLineSegment(sketch, "E36.bottom", {"start": v(0.1, 0.1) * mm, "end": v(1.1, 0.1) * mm});
            skLineSegment(sketch, "E36.top", {"start": v(0.1, 4.1) * mm, "end": v(1.1, 4.1) * mm});
            skLineSegment(sketch, "E36.left", {"start": v(0.1, 0.1) * mm, "end": v(0.1, 4.1) * mm});
            skLineSegment(sketch, "E36.right", {"start": v(1.1, 0.1) * mm, "end": v(1.1, 4.1) * mm});
            skSolve(sketch);
        }
        {
            var Q0;
            Q0=makeQuery(id+"F16.imprint","IMPRINT",FACE,{"disambiguationData":[TD([[makeQuery(id+"F16.imprint","IMPRINT",EDGE,{"derivedFrom":sQuery(id+"F16.wireOp",EDGE,"E36.bottom")}),1.0]])]});
            extrude(context, id + "F17", {"entities" : qUnion([Q0]), "operationType" : NewBodyOperationType.REMOVE, "oppositeDirection" : true, "depth" : 0.2 * mm, "offsetDistance" : 25 * mm});
        }
        {
            var Q0;
            {var subQ0=sQuery(id+"F0.wireOp",EDGE,"E4");var subQ1=sQuery(id+"F0.wireOp",EDGE,"E1");var subQ2=makeQuery(id+"F0.imprint","INTERSECT",VERTEX,{"derivedFrom":[subQ1,subQ0]});Q0=makeQuery(id+"F0.imprint","IMPRINT",FACE,{"disambiguationData":[TD([[makeQuery(id+"F0.imprint","IMPRINT",EDGE,{"disambiguationData":[TD([[subQ2,-1.0]])],"derivedFrom":subQ1}),1.0]])]});}
            var sketch = newSketch(context, id + "F18", { "sketchPlane" : qUnion([Q0])});
            skLineSegment(sketch, "E37.bottom", {"start": v(0, 50) * mm, "end": v(0.1, 50) * mm});
            skLineSegment(sketch, "E37.top", {"start": v(0, 0) * mm, "end": v(0.1, 0) * mm});
            skLineSegment(sketch, "E37.left", {"start": v(0, 50) * mm, "end": v(0, 0) * mm});
            skLineSegment(sketch, "E37.right", {"start": v(0.1, 50) * mm, "end": v(0.1, 0) * mm});
            skSolve(sketch);
        }
        {
            var Q0;
            Q0=makeQuery(id+"F18.imprint","IMPRINT",FACE,{"disambiguationData":[TD([[makeQuery(id+"F18.imprint","IMPRINT",EDGE,{"derivedFrom":sQuery(id+"F18.wireOp",EDGE,"E37.bottom")}),-1.0]])]});
            extrude(context, id + "F19", {"entities" : qUnion([Q0]), "operationType" : NewBodyOperationType.ADD, "depth" : 0.6 * mm, "offsetDistance" : 25 * mm});
        }
        {
            var Q0;
            Q0=makeQuery(id+"F13.opExtrude","CAP_FACE",FACE,{"disambiguationData":[OSD([sQuery(id+"F12.wireOp",EDGE,"E34.bottom"),sQuery(id+"F12.wireOp",EDGE,"E34.top"),sQuery(id+"F12.wireOp",EDGE,"E34.left"),sQuery(id+"F12.wireOp",EDGE,"E34.right")])],"isStart":false});
            var sketch = newSketch(context, id + "F20", { "sketchPlane" : qUnion([Q0])});
            skLineSegment(sketch, "E38", {"start": v(0.1, 4.2) * mm, "end": v(1.2, 4.2) * mm});
            skLineSegment(sketch, "E39", {"start": v(1.2, 4.2) * mm, "end": v(1.2, 1.1) * mm});
            skLineSegment(sketch, "E40", {"start": v(1.2, 1.1) * mm, "end": v(1.1, 1.1) * mm});
            skSolve(sketch);
        }
        {
            var Q0;
            {var subQ2=sQuery(id+"F20.wireOp",EDGE,"E38");Q0=makeQuery(id+"F20.imprint","IMPRINT",FACE,{"disambiguationData":[TD([[makeQuery(id+"F20.imprint","IMPRINT",EDGE,{"derivedFrom":subQ2}),-1.0]])]});}
            extrude(context, id + "F21", {"entities" : qUnion([Q0]), "operationType" : NewBodyOperationType.ADD, "depth" : 1 * mm, "offsetDistance" : 25 * mm});
        }
    });
